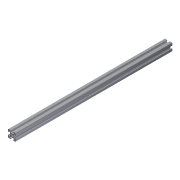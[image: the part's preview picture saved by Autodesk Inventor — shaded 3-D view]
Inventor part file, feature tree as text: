
AUTODESK INVENTOR PART (.ipt)
format: ipt  version: 2011 (Build 150239000, 239)  size: 386,560 bytes
history: native  units: in
note: dims shown in document units (in); Inventor stores cm internally (conversion verified against a paired STEP export)
features: extrude x3, sketch x3
ambient origin geometry x8: Origin, YZ Plane, XZ Plane, XY Plane, X Axis, Y Axis, Z Axis, Center Point
bodies: Solid1 (feature_tree)
feature tree (6):
  extrude  "Extrusion1"  Depth=1.3937in TaperAngle=0.0deg
  extrude  "Extrusion2"  [1 undecoded]
  extrude  "Extrusion3"  [1 undecoded]
  sketch  "Sketch1"  dims[d0=17.5in d1=0.0in d2=1.3937in d3=0.0in]
  sketch  "Sketch2"  dims[d4=1.3937in d5=0.0in]
  sketch  "Sketch3"
note: 2 required parameter values undecoded (feature->parameter linkage not recoverable at this tier; creation-order binding heuristic only, values carry confidence <= 0.55)
